# Revit family: B 0375 SLS - ASM-L4
name_source: partatom
category: Lighting Fixtures
revit_build: Autodesk Revit 2017 (Build: 20160225_1515(x64)
units: mm (PartAtom-declared; Revit-internal decimal feet)

## family parameters
Cut with Voids When Loaded = No
Host = Face
Light Source = Yes
Part Type = Normal
Room Calculation Point = No
Round Connector Dimension = Use Diameter
Shared = No

## types (2) — shared parameters
Color Filter = 16777215
Default Elevation = 1219 mm
Description = Beam Angle : ASM-L4
Dimming Lamp Color Temperature Shift = <None>
Emit Shape Visible in Rendering = Yes
Emit from Rectangle Length = 229 mm
Emit from Rectangle Width = 205 mm  [stored 0.672572 ft]
Lamp = LED
Manufacturer = ARLIGHT AYDINLATMA
Model = B0375SLS
Tilt Angle = 90.00°
Type Comments = Floodlight
URL = www.arlight.net/en/products/outdoor-lighting-fixture/solis/b-0375-sls

## per-type parameters (varying)
| type | Apparent Load | Photometric Web File | Wattage Comments |
| BSLS.0375.140.40.ASL4 | 140 VA | b-0375-sls-140w-4k-70ra-e2sb-asym-l4-09.ies | 140W |
| BSLS.0375.105.40.ASL4 | 100 VA | b-0375-sls-105w-4k-70ra-e2sb-asym-l4-07.ies | 105W |

note: [stored X ft] marks values corroborated as IEEE doubles in the binary element streams (Revit-internal decimal feet)

## geometry (parser evidence)
native form markers: Sweep x2
no freeform markers — native parametric forms only
